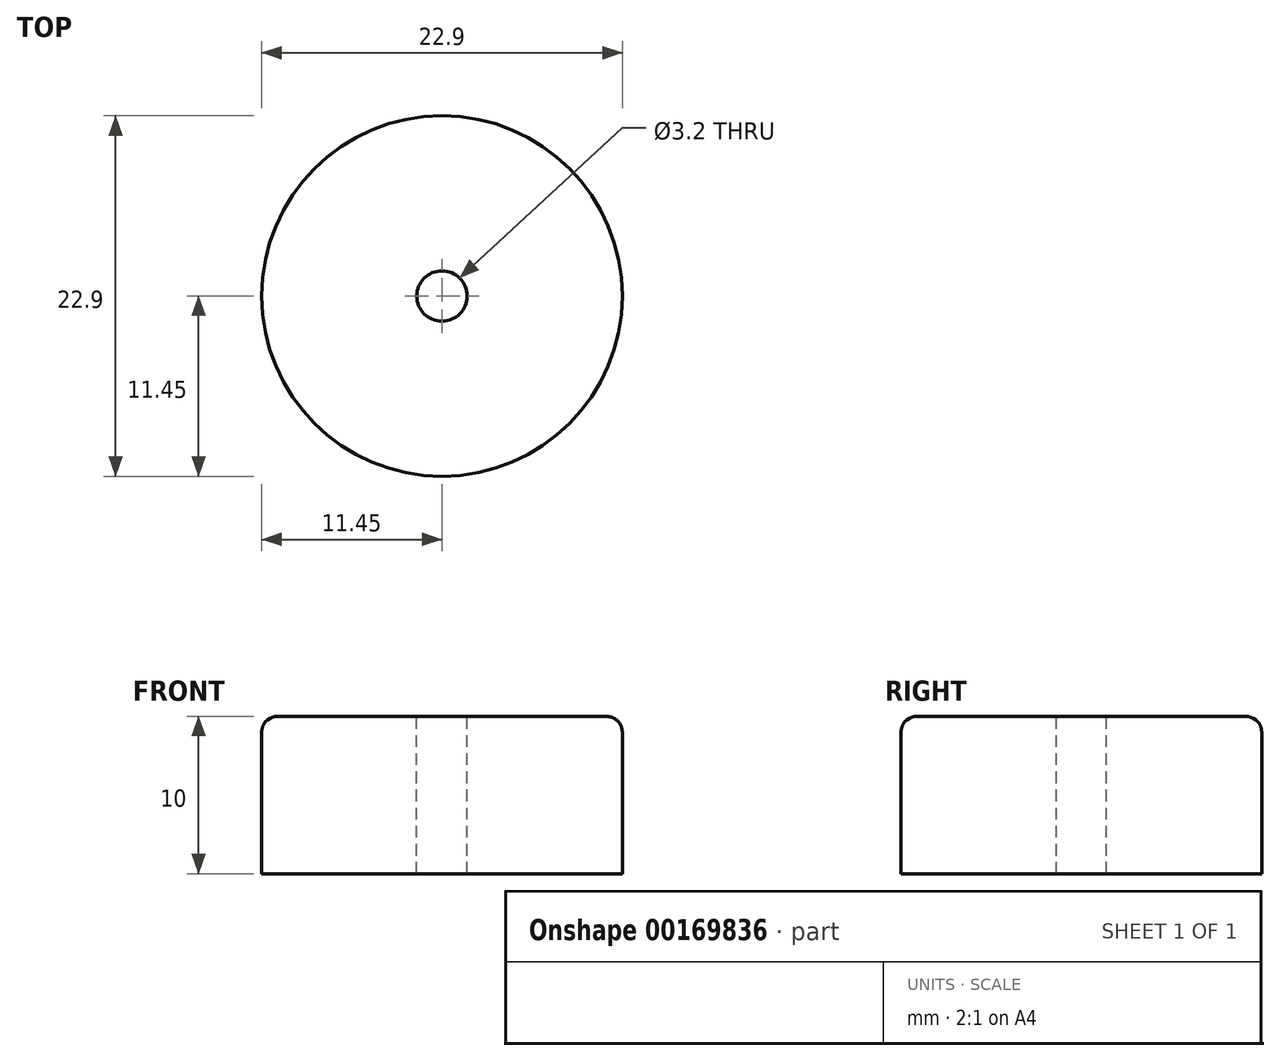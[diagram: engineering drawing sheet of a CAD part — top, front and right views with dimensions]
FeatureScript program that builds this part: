
annotation { "Feature Type Name" : "Feature", "Feature Type Description" : "" }
export const myFeature = defineFeature(function(context is Context, id is Id, definition is map)
    precondition{}
    {
        {
            var Q0;
            Q0=qCreatedBy(makeId("Top.planeOp"),FACE);
            var sketch = newSketch(context, id + "F0", { "sketchPlane" : qUnion([Q0])});
            skCircle(sketch, "E0", {"center": v(0, 0) * mm, "radius": 11.45 * mm});
            skCircle(sketch, "E1", {"center": v(0, 0) * mm, "radius": 1.6 * mm});
            skSolve(sketch);
        }
        {
            var Q0;
            Q0=qCreatedBy(makeId("Front.planeOp"),FACE);
            var sketch = newSketch(context, id + "F1", { "sketchPlane" : qUnion([Q0])});
            skLineSegment(sketch, "E2", {"start": v(0, 0) * mm, "end": v(0, 10) * mm});
            skSolve(sketch);
        }
        {
            var Q0;
            Q0=makeQuery(id+"F0.imprint","IMPRINT",FACE,{"disambiguationData":[TD([[makeQuery(id+"F0.imprint","IMPRINT",EDGE,{"derivedFrom":sQuery(id+"F0.wireOp",EDGE,"E0")}),1.0]])]});
            var Q1;
            Q1=sQuery(id+"F1.wireOp",EDGE,"E2");
            sweep(context, id + "F2", {"profiles" : qUnion([Q0]), "path" : qUnion([Q1])});
        }
        {
            var Q0;
            Q0=makeQuery(id+"F2.opSweep","CAP_EDGE",EDGE,{"disambiguationData":[OSD([sQuery(id+"F0.wireOp",EDGE,"E0"),sQuery(id+"F1.wireOp",VERTEX,"E2.end")])],"isStart":false});
            fillet(context, id + "F3", {"entities" : qUnion([Q0]), "radius" : 1 * mm, "allowEdgeOverflow" : false});
        }
    });
